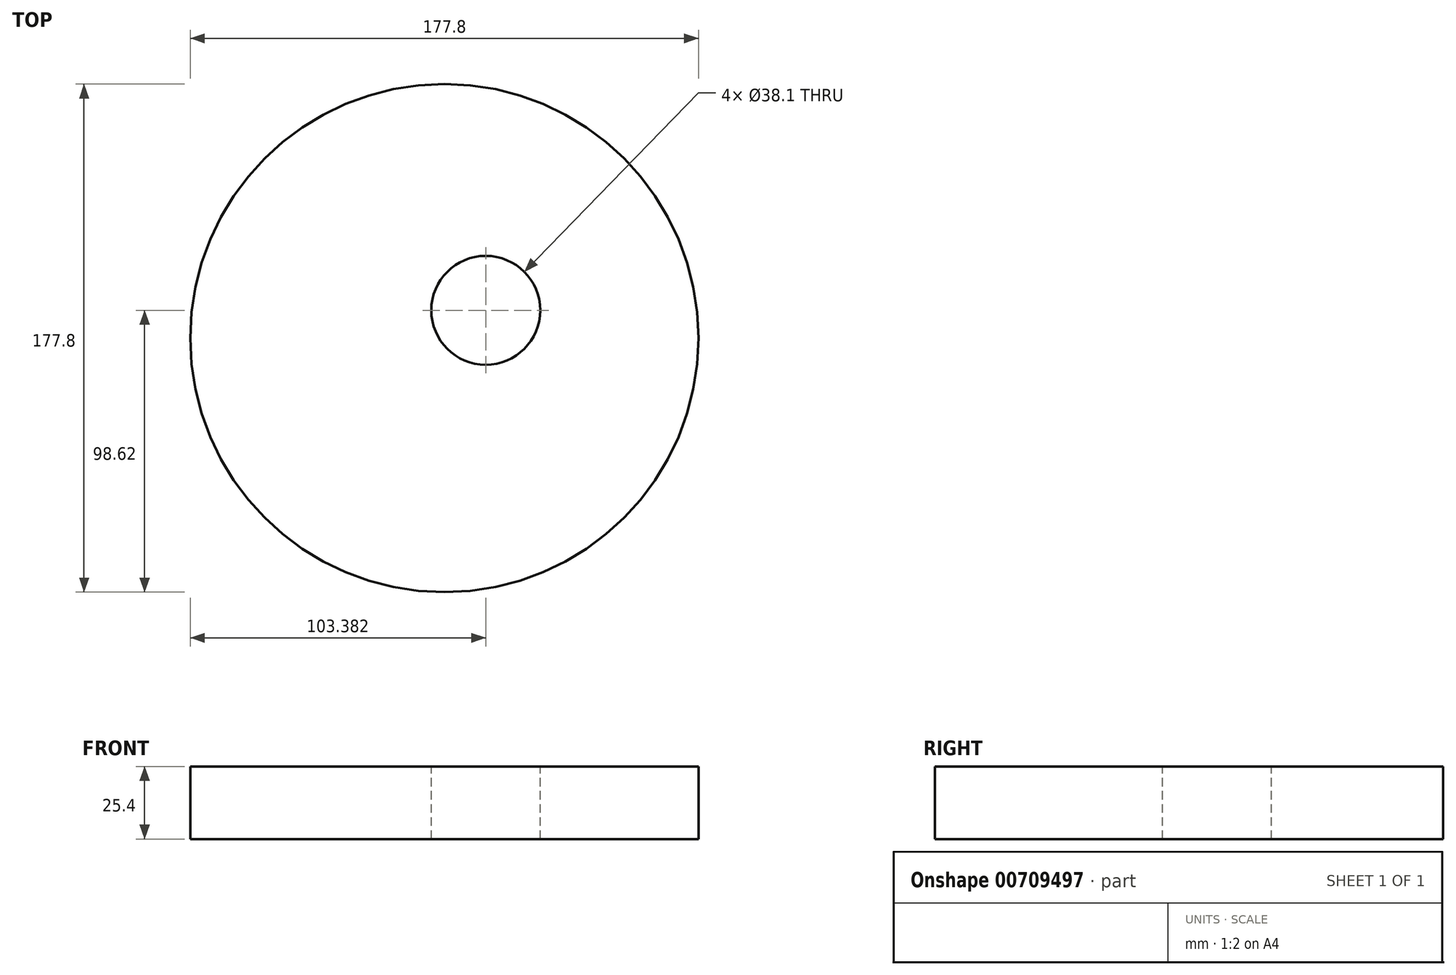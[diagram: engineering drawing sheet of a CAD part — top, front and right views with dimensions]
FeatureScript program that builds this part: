
annotation { "Feature Type Name" : "Feature", "Feature Type Description" : "" }
export const myFeature = defineFeature(function(context is Context, id is Id, definition is map)
    precondition{}
    {
        {
            var Q0;
            Q0=qCreatedBy(makeId("Top.planeOp"),FACE);
            var sketch = newSketch(context, id + "F0", { "sketchPlane" : qUnion([Q0])});
            skCircle(sketch, "E0", {"center": v(-50.9, 41.08) * mm, "radius": 88.9 * mm});
            skSolve(sketch);
        }
        {
            var Q0;
            Q0 = qSketchRegion(id + "F0", true);
            extrude(context, id + "F1", {"entities" : qUnion([Q0]), "depth" : 25.4 * mm, "offsetDistance" : 25.4 * mm});
        }
        {
            var Q0;
            Q0=makeQuery(id+"F1.opExtrude","CAP_FACE",FACE,{"disambiguationData":[OSD([sQuery(id+"F0.wireOp",EDGE,"E0")])],"isStart":false});
            var sketch = newSketch(context, id + "F2", { "sketchPlane" : qUnion([Q0])});
            skCircle(sketch, "E1", {"center": v(-36.42, 50.8) * mm, "radius": 19.05 * mm});
            skSolve(sketch);
        }
        {
            var Q0;
            Q0=makeQuery(id+"F2.imprint","IMPRINT",FACE,{"disambiguationData":[TD([[makeQuery(id+"F2.imprint","IMPRINT",EDGE,{"derivedFrom":sQuery(id+"F2.wireOp",EDGE,"E1")}),1.0]])]});
            var Q1;
            Q1=sQuery(id+"F2.wireOp",EDGE,"E1");
            extrude(context, id + "F3", {"entities" : qUnion([Q0]), "operationType" : NewBodyOperationType.REMOVE, "surfaceEntities" : qUnion([Q1]), "oppositeDirection" : true, "depth" : 25.4 * mm, "offsetDistance" : 25.4 * mm});
        }
    });
